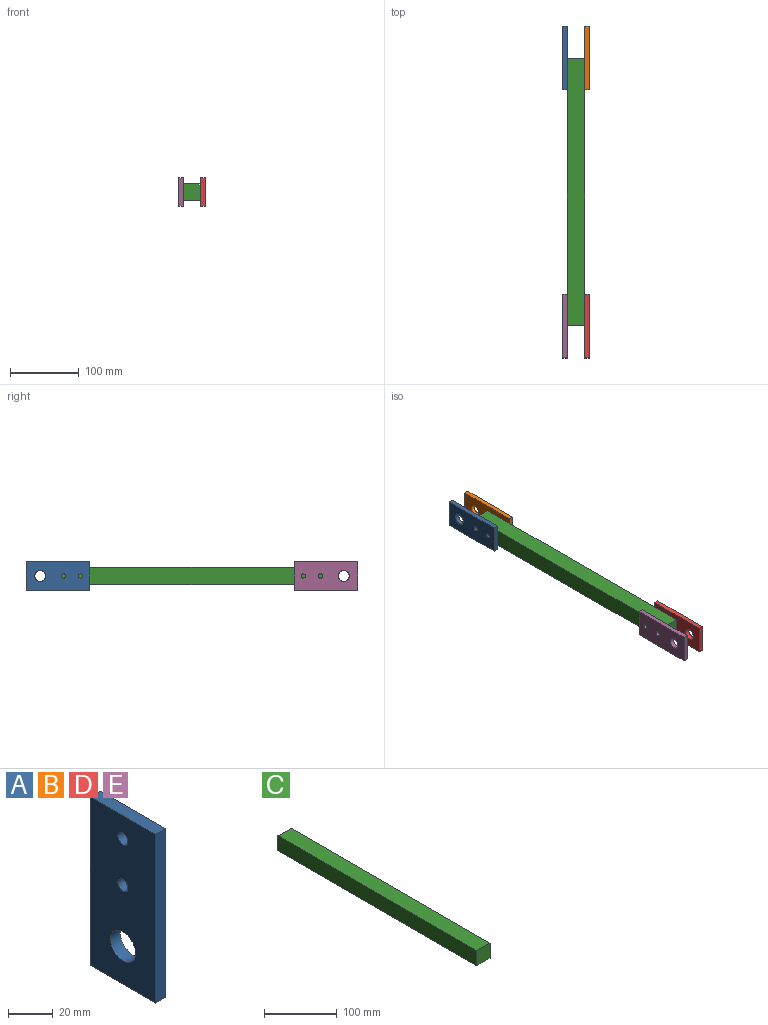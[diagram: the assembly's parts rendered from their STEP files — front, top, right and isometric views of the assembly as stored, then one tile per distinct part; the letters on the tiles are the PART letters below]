
ASSEMBLY  parts=5 mates=4
PART A: 9 faces, bbox 6.4x41.3x92.1 mm
  f0: plane 92.08x6.35mm, normal (0,-1,0), area 584.7mm2, adj f1,f3,f7,f8
  f1: plane 41.28x6.35mm, normal (0,0,-1), area 262.1mm2, adj f0,f2,f7,f8
  f2: plane 92.08x6.35mm, normal (0,1,0), area 584.7mm2, adj f1,f3,f7,f8
  f3: plane 41.28x6.35mm, normal (0,0,1), area 262.1mm2, adj f0,f2,f7,f8
  f4: cylinder r=3.17mm len=6.35mm, axis (-1,0,0), area 126.7mm2, adj f7,f8
  f5: cylinder r=3.17mm len=6.35mm, axis (-1,0,0), area 126.7mm2, adj f7,f8
  f6: cylinder r=7.94mm len=15.88mm, axis (-1,0,0), area 316.7mm2, adj f7,f8
  f7: plane 92.08x41.28mm, normal (1,0,0), area 3539.1mm2, adj f0,f1,f2,f3,f4,f5,f6
  f8: plane 92.08x41.28mm, normal (-1,0,0), area 3539.1mm2, adj f0,f1,f2,f3,f4,f5,f6
PART B: same geometry as A
PART C: 6 faces, bbox 25.4x387x25.4 mm
  f0: plane 387.03x25.4mm, normal (1,0,0), area 9830.5mm2, adj f1,f3,f4,f5
  f1: plane 387.03x25.4mm, normal (0,0,1), area 9830.5mm2, adj f0,f2,f4,f5
  f2: plane 387.03x25.4mm, normal (-1,0,0), area 9830.5mm2, adj f1,f3,f4,f5
  f3: plane 387.03x25.4mm, normal (0,0,-1), area 9830.5mm2, adj f0,f2,f4,f5
  f4: plane 25.4x25.4mm, normal (0,-1,0), area 645.2mm2, adj f0,f1,f2,f3
  f5: plane 25.4x25.4mm, normal (0,1,0), area 645.2mm2, adj f0,f1,f2,f3
PART D: same geometry as A
PART E: same geometry as A
PLACE A rot(axis=(0,-0.71,0.71),180deg) t=(-81.13,154.13,23.63)mm
PLACE B rot(axis=(0,-0.71,0.71),180deg) t=(-49.38,154.13,23.63)mm
PLACE C t=(-65.25,-45.2,2.99)mm
PLACE D rot(axis=(0,-0.71,-0.71),180deg) t=(-49.38,-244.53,-17.64)mm
PLACE E rot(axis=(0,-0.71,-0.71),180deg) t=(-81.13,-244.53,-17.64)mm
MATE fastened E.f8 <-> C.f2  axis (1,0,0) through (-77.95,-238.71,2.99)mm
MATE fastened B.f7 <-> C.f0  axis (-1,0,0) through (-52.55,148.31,2.99)mm
MATE fastened A.f8 <-> C.f2  axis (1,0,0) through (-77.95,148.31,2.99)mm
MATE fastened D.f7 <-> C.f0  axis (-1,0,0) through (-52.55,-238.71,2.99)mm
